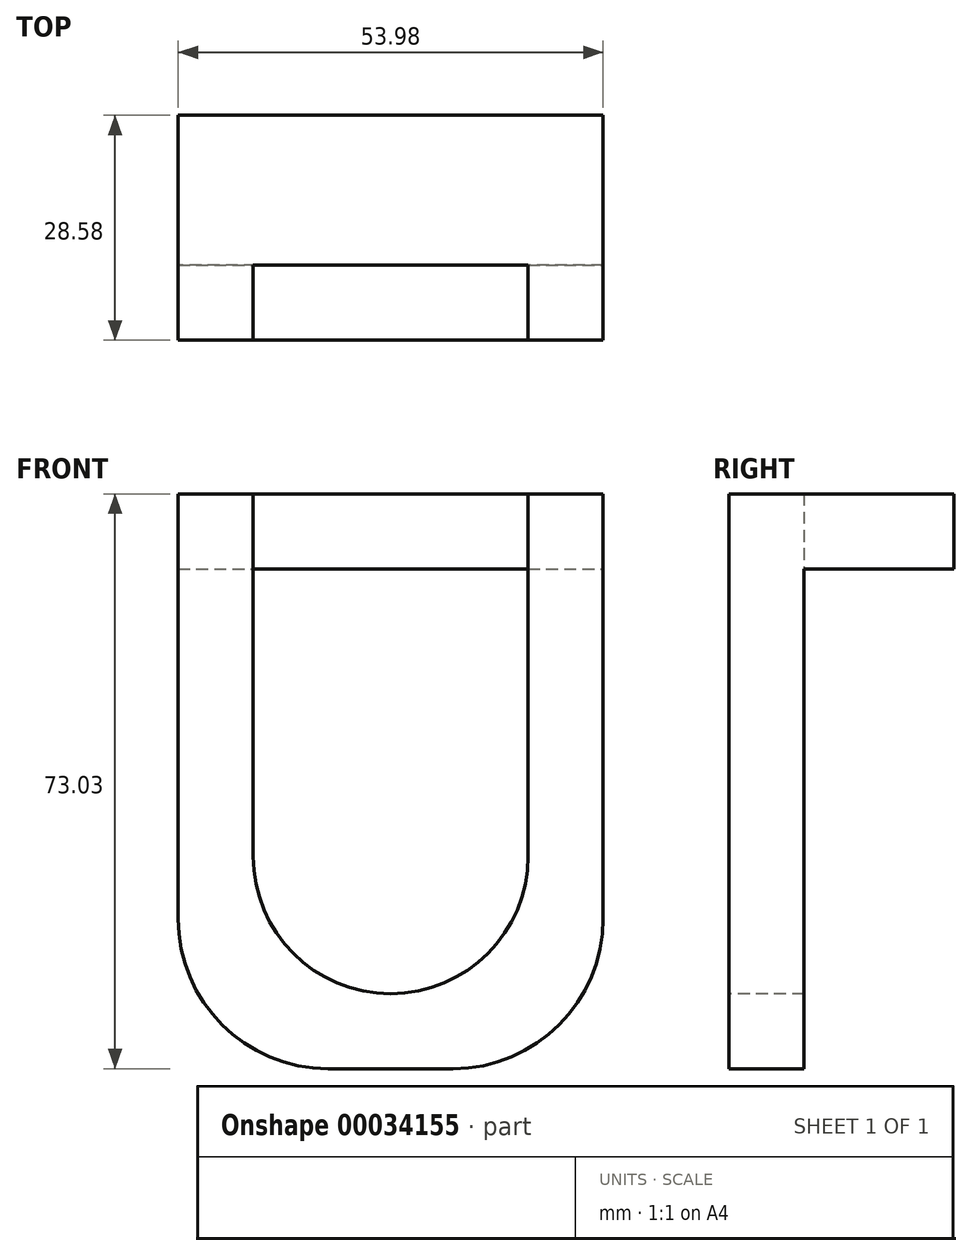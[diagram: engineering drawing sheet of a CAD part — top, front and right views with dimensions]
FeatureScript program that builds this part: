
annotation { "Feature Type Name" : "Feature", "Feature Type Description" : "" }
export const myFeature = defineFeature(function(context is Context, id is Id, definition is map)
    precondition{}
    {
        {
            var Q0;
            Q0=qCreatedBy(makeId("Top.planeOp"),FACE);
            var sketch = newSketch(context, id + "F0", { "sketchPlane" : qUnion([Q0])});
            skLineSegment(sketch, "E0.bottom", {"start": v(-26.99, 0) * mm, "end": v(26.99, 0) * mm});
            skLineSegment(sketch, "E0.top", {"start": v(-26.99, 19.05) * mm, "end": v(26.99, 19.05) * mm});
            skLineSegment(sketch, "E0.left", {"start": v(-26.99, 0) * mm, "end": v(-26.99, 19.05) * mm});
            skLineSegment(sketch, "E0.right", {"start": v(26.99, 0) * mm, "end": v(26.99, 19.05) * mm});
            skSolve(sketch);
        }
        {
            var Q0;
            Q0=makeQuery(id+"F0.imprint","IMPRINT",FACE,{"disambiguationData":[TD([[makeQuery(id+"F0.imprint","IMPRINT",EDGE,{"derivedFrom":sQuery(id+"F0.wireOp",EDGE,"E0.bottom")}),1.0]])]});
            extrude(context, id + "F1", {"entities" : qUnion([Q0]), "depth" : 9.52 * mm});
        }
        {
            var Q0;
            Q0=qCreatedBy(makeId("Top.planeOp"),FACE);
            var sketch = newSketch(context, id + "F2", { "sketchPlane" : qUnion([Q0])});
            skLineSegment(sketch, "E1.bottom", {"start": v(-26.99, 0) * mm, "end": v(26.99, 0) * mm});
            skLineSegment(sketch, "E1.top", {"start": v(-26.99, -9.53) * mm, "end": v(26.99, -9.53) * mm});
            skLineSegment(sketch, "E1.left", {"start": v(-26.99, 0) * mm, "end": v(-26.99, -9.52) * mm});
            skLineSegment(sketch, "E1.right", {"start": v(26.99, 0) * mm, "end": v(26.99, -9.52) * mm});
            skSolve(sketch);
        }
        {
            var Q0;
            Q0=makeQuery(id+"F2.imprint","IMPRINT",FACE,{"disambiguationData":[TD([[makeQuery(id+"F2.imprint","IMPRINT",EDGE,{"derivedFrom":sQuery(id+"F2.wireOp",EDGE,"E1.bottom")}),-1.0]])]});
            extrude(context, id + "F3", {"entities" : qUnion([Q0]), "operationType" : NewBodyOperationType.ADD, "depth" : 9.52 * mm, "hasSecondDirection" : true, "secondDirectionOppositeDirection" : true, "secondDirectionDepth" : 63.5 * mm});
        }
        {
            var Q0;
            Q0=makeQuery(id+"F3.opExtrude","SWEPT_FACE",FACE,{"disambiguationData":[OSD([sQuery(id+"F2.wireOp",EDGE,"E1.top")])]});
            var sketch = newSketch(context, id + "F4", { "sketchPlane" : qUnion([Q0])});
            skLineSegment(sketch, "E2", {"start": v(-17.46, 9.53) * mm, "end": v(17.46, 9.53) * mm});
            skLineSegment(sketch, "E3", {"start": v(17.46, 9.53) * mm, "end": v(17.46, -36.51) * mm});
            skLineSegment(sketch, "E4", {"start": v(-17.46, -36.51) * mm, "end": v(-17.46, 9.53) * mm});
            skArc(sketch, "E5", {"start": v(-17.46, -36.51) * mm, "mid": v(0, -53.98) * mm, "end": v(17.46, -36.51) * mm});
            skPoint(sketch, "E6", {"position": v(0, -53.98) * mm});
            skSolve(sketch);
        }
        {
            var Q0;
            Q0 = qSketchRegion(id + "F4", true);
            extrude(context, id + "F5", {"entities" : qUnion([Q0]), "operationType" : NewBodyOperationType.REMOVE, "oppositeDirection" : true, "depth" : 9.52 * mm});
        }
        {
            var Q0;
            Q0=makeQuery(id+"F3.opExtrude","CAP_EDGE",EDGE,{"disambiguationData":[OSD([sQuery(id+"F2.wireOp",EDGE,"E1.right")])],"isStart":true});
            var Q1;
            Q1=makeQuery(id+"F3.opExtrude","CAP_EDGE",EDGE,{"disambiguationData":[OSD([sQuery(id+"F2.wireOp",EDGE,"E1.left")])],"isStart":true});
            fillet(context, id + "F6", {"entities" : qUnion([Q0, Q1]), "radius" : 19.05 * mm, "tangentPropagation" : true, "allowEdgeOverflow" : false});
        }
    });
